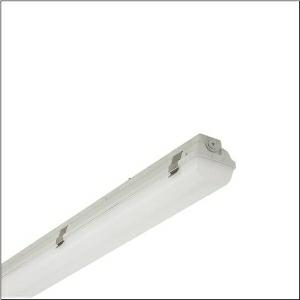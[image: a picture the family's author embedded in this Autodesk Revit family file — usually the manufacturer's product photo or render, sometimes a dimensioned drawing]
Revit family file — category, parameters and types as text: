
# Revit family: monsun_r__21_eco_51fj10dp47a_8000
name_source: partatom
category: Lighting Fixtures
units: mm (PartAtom-declared; Revit-internal decimal feet)

## family parameters
Cut with Voids When Loaded = No
Host = Face
Light Source = No
Part Type = Normal
Room Calculation Point = No
Round Connector Dimension = Use Diameter
Shared = No

## types (1)
- Monsun® 21 Eco (1 x LED, 7000 lm, 50 W, 4000K)
    Apparent Load = 50 VA
    CIE Flux Codes = 41 70 89 90 100
    Color Rendering = 80
    Color Temperature = 4000K
    Default Elevation = 1800 mm
    Description = Monsun® 21 Eco, damp-proof luminaire, primary optical cover: diffuser, of PMMA, frosted, light emission: direct distribution, primary light characteristic: symmetric, installation type: suspended mounting, surface-mounted, LED, rated luminous flux: 7.000lm, luminous efficacy: 140lm/W, light colour: 840, colour temperature: 4000K, control gear: ECG DALI, with terminal, 5-pole, max. 2.5mm², mains connection: 220..240V, AC, 50/60Hz, rated input power: 50W, housing, of glass-fibre reinforced polyester, light grey (RAL 7035), length: 1.577mm, width: 90mm, height: 95mm, clip for enclosure, of spring steel V2A, protection rating (complete): IP66, insulation class (complete): insulation class I (protective earthing), certification: CE, UKCA, protection symbol: D, impact resistance: IK02, permissible operating ambient temperature: -20..+35°C, corresponds to IFS (International Featured Standards) requirements for safety and quality in the food industry, packaging unit: 1 piece
    Height = 103 mm
    Lamp = 1 x LED
    Lamp Light Flux = 7000 lm
    Lamp Power = 50 W
    Lamp count = 1
    Length = 1577 mm
    Luminous efficacy = 140 lm/W
    Manufacturer = Siteco
    ModVariant = No
    Model = 51FJ10DP47A
    Mounting Place = Ceiling
    Mounting Type = Surface mounted
    Number of Poles = 1
    OnlyDefault = Yes
    Power Factor = 1
    Product Name = Monsun® 21 Eco
    Product group = damp-proof luminaire | ceiling mounted
    ProductGroupID = 300
    Protection Class = Protection class I
    Protection Degree = IP 66
    RLX_Detail_Level = 1
    RlxData = <blob elided: 33257 chars, md5=209e0dc9>
    Socket = socket
    Standby Power = 0 W
    System Light Flux = 7000 lm
    System Power = 50 W
    Type Comments = Product without accessories
    Type Image = l_1007218.jpg
    URL = http://relux.com
    VarID = ---
    Voltage = 0 V
    Weight = 0.00 kg
    Width = 90 mm

## geometry (parser evidence)
native form markers: Blend x4, Sweep x10
no freeform markers — native parametric forms only
